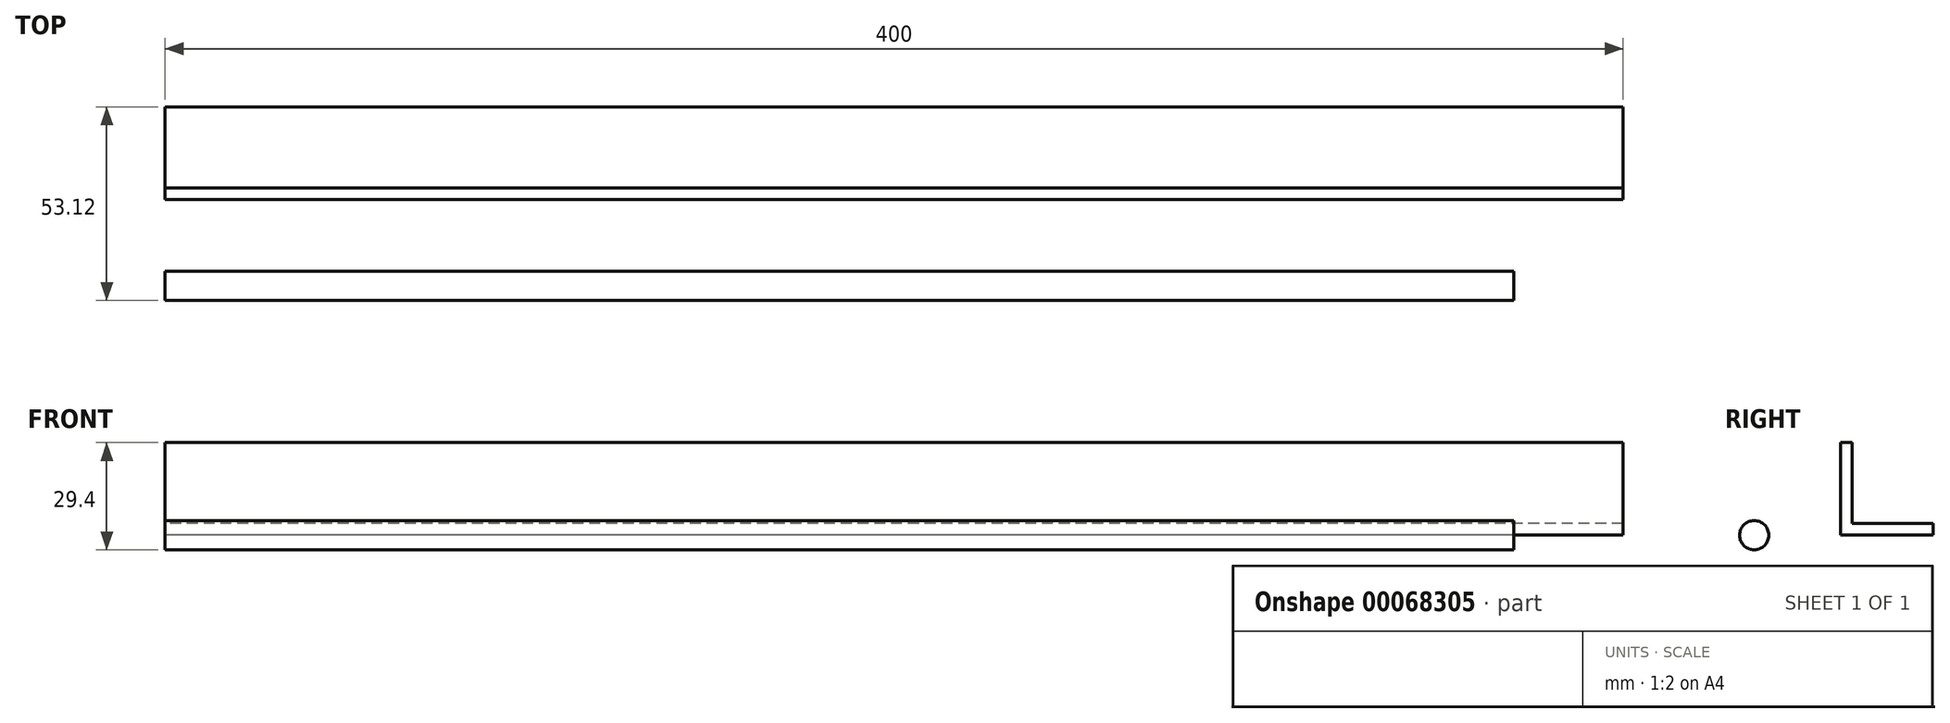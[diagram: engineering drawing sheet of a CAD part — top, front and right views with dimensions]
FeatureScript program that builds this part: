
annotation { "Feature Type Name" : "Feature", "Feature Type Description" : "" }
export const myFeature = defineFeature(function(context is Context, id is Id, definition is map)
    precondition{}
    {
        {
            var Q0;
            Q0=qCreatedBy(makeId("Right.planeOp"),FACE);
            var sketch = newSketch(context, id + "F0", { "sketchPlane" : qUnion([Q0])});
            skCircle(sketch, "E0", {"center": v(0, 0) * mm, "radius": 4 * mm});
            skSolve(sketch);
        }
        {
            var Q0;
            Q0 = qSketchRegion(id + "F0", true);
            extrude(context, id + "F1", {"entities" : qUnion([Q0]), "depth" : 370 * mm});
        }
        {
            var Q0;
            Q0=qCreatedBy(makeId("Right.planeOp"),FACE);
            var sketch = newSketch(context, id + "F2", { "sketchPlane" : qUnion([Q0])});
            skLineSegment(sketch, "E1", {"start": v(23.72, 0) * mm, "end": v(49.12, 0) * mm});
            skLineSegment(sketch, "E2", {"start": v(49.12, 0) * mm, "end": v(49.12, 3.17) * mm});
            skLineSegment(sketch, "E3", {"start": v(49.12, 3.18) * mm, "end": v(26.9, 3.17) * mm});
            skLineSegment(sketch, "E4", {"start": v(26.9, 3.17) * mm, "end": v(26.9, 25.4) * mm});
            skLineSegment(sketch, "E5", {"start": v(26.9, 25.4) * mm, "end": v(23.72, 25.4) * mm});
            skLineSegment(sketch, "E6", {"start": v(23.72, 25.4) * mm, "end": v(23.72, 0) * mm});
            skSolve(sketch);
        }
        {
            var Q0;
            Q0 = qSketchRegion(id + "F2", true);
            extrude(context, id + "F3", {"entities" : qUnion([Q0]), "depth" : 400 * mm});
        }
    });
